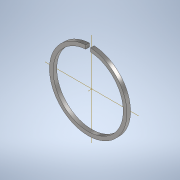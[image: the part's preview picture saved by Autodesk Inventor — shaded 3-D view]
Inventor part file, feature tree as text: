
AUTODESK INVENTOR PART (.ipt)
format: ipt  version: 2021.1 (Build 251245000, 245)  size: 117,248 bytes
history: native  units: in
note: dims shown in document units (in); Inventor stores cm internally (conversion verified against a paired STEP export)
features: extrude x1, sketch x1
ambient origin geometry x8: Origin, YZ Plane, XZ Plane, XY Plane, X Axis, Y Axis, Z Axis, Center Point
bodies: Solid1 (feature_tree)
feature tree (2):
  extrude  "Extrusion1"  Depth=0.15in
  sketch  "Sketch1"  dims[d0=2.9in d1=3.2in d2=0.2in d3=0.15in d4=0.0in]
